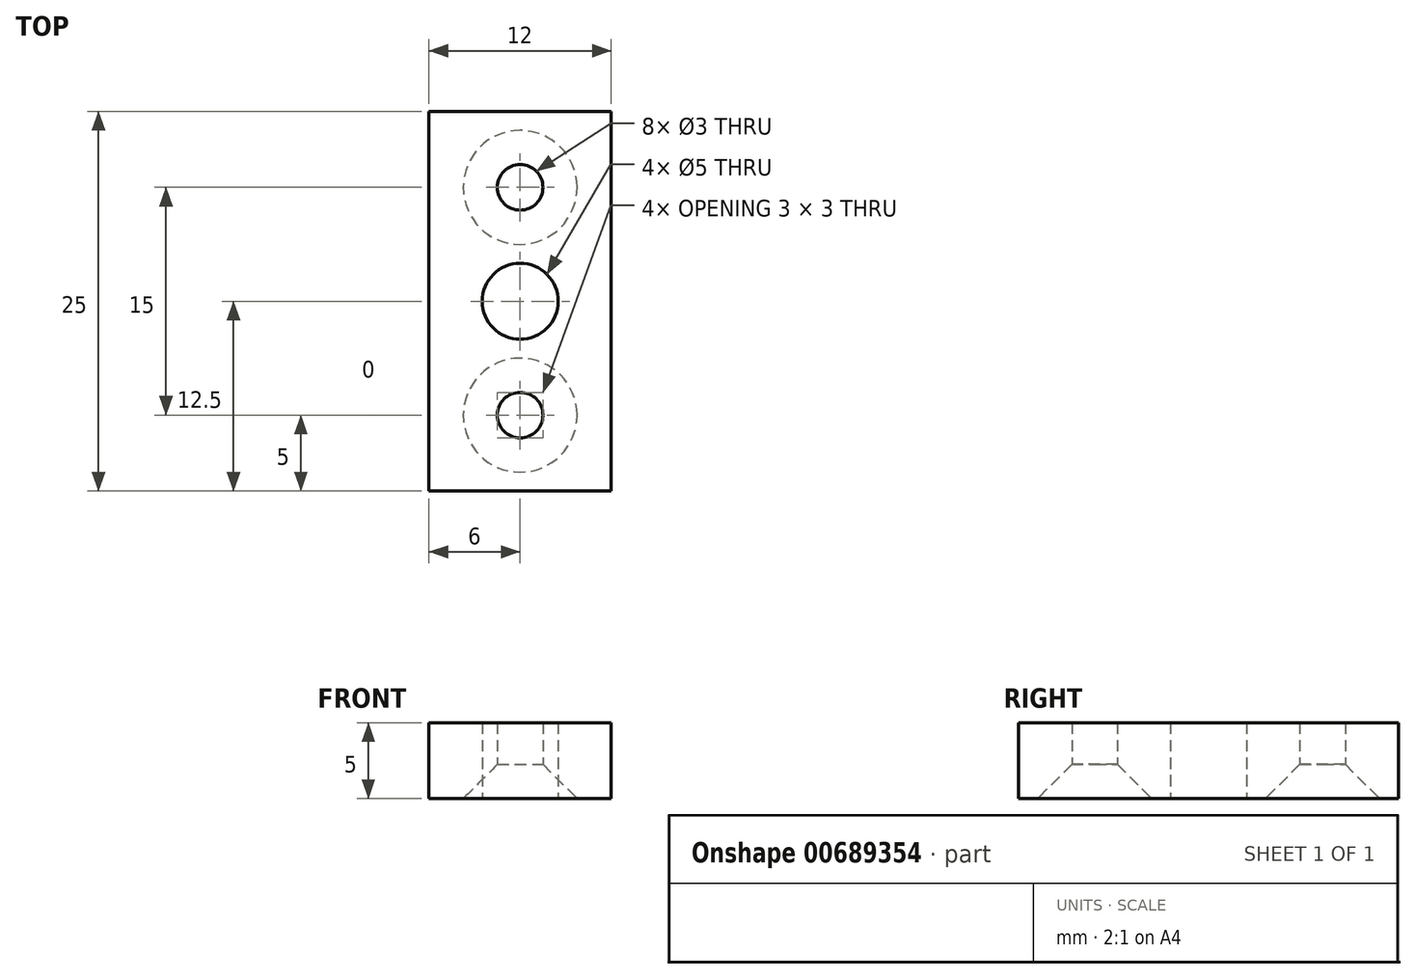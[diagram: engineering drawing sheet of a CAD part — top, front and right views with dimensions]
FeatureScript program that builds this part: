
annotation { "Feature Type Name" : "Feature", "Feature Type Description" : "" }
export const myFeature = defineFeature(function(context is Context, id is Id, definition is map)
    precondition{}
    {
        {
            var Q0;
            Q0=qCreatedBy(makeId("Top.planeOp"),FACE);
            var sketch = newSketch(context, id + "F0", { "sketchPlane" : qUnion([Q0])});
            skCircle(sketch, "E0", {"center": v(0, 0) * mm, "radius": 2.5 * mm});
            skLineSegment(sketch, "E1.bottom", {"start": v(6, 12.5) * mm, "end": v(-6, 12.5) * mm});
            skLineSegment(sketch, "E1.top", {"start": v(6, -12.5) * mm, "end": v(-6, -12.5) * mm});
            skLineSegment(sketch, "E1.left", {"start": v(6, 12.5) * mm, "end": v(6, -12.5) * mm});
            skLineSegment(sketch, "E1.right", {"start": v(-6, 12.5) * mm, "end": v(-6, -12.5) * mm});
            skSolve(sketch);
        }
        {
            var Q0;
            Q0=qSketchRegion(id+"F0",true);
            extrude(context, id + "F1", {"entities" : qUnion([Q0]), "depth" : 5 * mm, "offsetDistance" : 25 * mm});
        }
        {
            var Q0;
            Q0=makeQuery(id+"F1.opExtrude","CAP_FACE",FACE,{"disambiguationData":[OSD([sQuery(id+"F0.wireOp",EDGE,"E0"),sQuery(id+"F0.wireOp",EDGE,"E1.bottom"),sQuery(id+"F0.wireOp",EDGE,"E1.top"),sQuery(id+"F0.wireOp",EDGE,"E1.left"),sQuery(id+"F0.wireOp",EDGE,"E1.right")])],"isStart":true});
            var sketch = newSketch(context, id + "F2", { "sketchPlane" : qUnion([Q0])});
            skPoint(sketch, "E2", {"position": v(0, 7.5) * mm});
            skPoint(sketch, "E3", {"position": v(0, -7.5) * mm});
            skSolve(sketch);
        }
        {
            var Q0;
            Q0=sQuery(id+"F2.wireOp",VERTEX,"E2");
            var Q1;
            Q1=sQuery(id+"F2.wireOp",VERTEX,"E3");
            var Q2;
            Q2=makeQuery(id+"F1.opExtrude","SWEPT_BODY",BODY,{"disambiguationData":[OSD([sQuery(id+"F0.wireOp",EDGE,"E0"),sQuery(id+"F0.wireOp",EDGE,"E1.bottom"),sQuery(id+"F0.wireOp",EDGE,"E1.top"),sQuery(id+"F0.wireOp",EDGE,"E1.left"),sQuery(id+"F0.wireOp",EDGE,"E1.right")])]});
            hole(context, id + "F3", {"style" : HoleStyle.C_SINK, "endStyle" : HoleEndStyle.THROUGH, "holeDiameter" : 3 * mm, "cSinkDiameter" : 7.5 * mm, "cSinkAngle" : 90 * degree, "majorDiameter" : 5 * mm, "isTappedThrough" : true, "tappedDepth" : 12 * mm, "tapClearance" : 3, "startFromSketch" : true, "locations" : qUnion([Q0, Q1]), "scope" : qUnion([Q2])});
        }
    });
